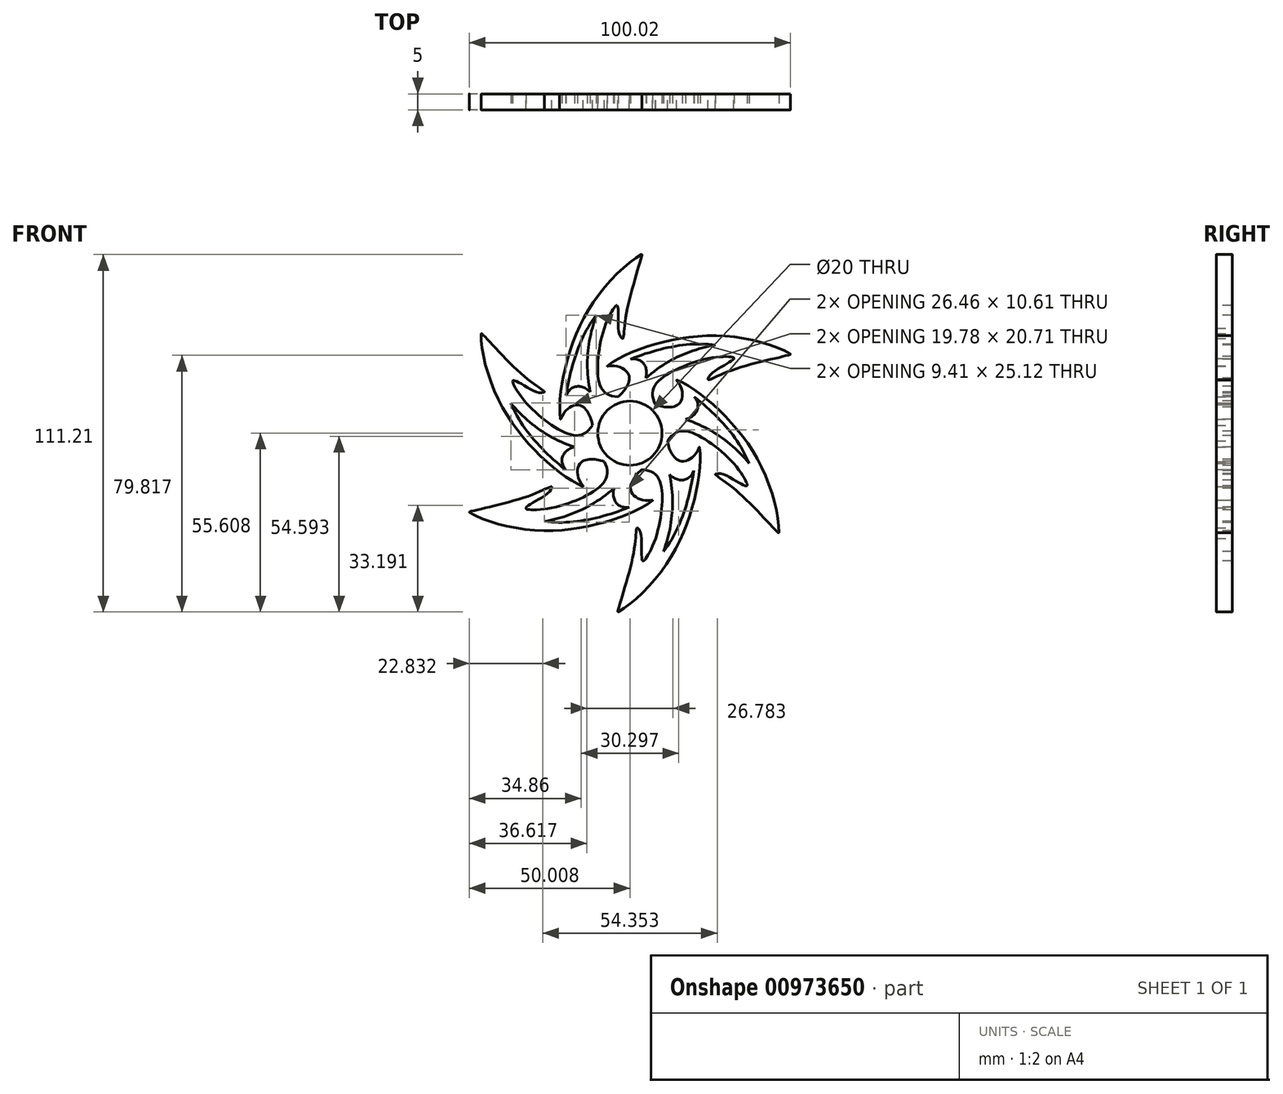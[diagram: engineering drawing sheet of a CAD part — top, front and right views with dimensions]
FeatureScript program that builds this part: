
annotation { "Feature Type Name" : "Feature", "Feature Type Description" : "" }
export const myFeature = defineFeature(function(context is Context, id is Id, definition is map)
    precondition{}
    {
        {
            var Q0;
            Q0=qCreatedBy(makeId("Front.planeOp"),FACE);
            var sketch = newSketch(context, id + "F0", { "sketchPlane" : qUnion([Q0])});
            skArc(sketch, "E0", {"start": v(51.43, 69.64) * mm, "mid": v(53.41, 47.38) * mm, "end": v(64.36, 66.87) * mm});
            skFitSpline(sketch, "E1", {"points": [v(51.43, 69.64) * mm, v(54.7, 73.05) * mm, v(55.5, 76.92) * mm, v(48.53, 79.55) * mm], "startDerivative": vector(15.23, 10.38) * mm, "endDerivative": vector(-26.97, -6.76) * mm});
            skFitSpline(sketch, "E2", {"points": [v(48.53, 79.55) * mm, v(62.9, 86.26) * mm, v(85.86, 89) * mm, v(106.01, 83.36) * mm], "startDerivative": vector(30.67, 25.16) * mm, "endDerivative": vector(38.45, -24.26) * mm});
            skFitSpline(sketch, "E3", {"points": [v(80.2, 75.5) * mm, v(87.2, 78.3) * mm, v(106.01, 83.36) * mm], "startDerivative": vector(3.98, -2.07) * mm, "endDerivative": vector(10.42, 3.53) * mm});
            skFitSpline(sketch, "E4", {"points": [v(80.2, 75.5) * mm, v(85.84, 80.3) * mm, v(88.27, 82.15) * mm, v(87.74, 82.5) * mm, v(80.2, 82.1) * mm], "startDerivative": vector(1.03, 17.3) * mm, "endDerivative": vector(-30.04, -5.32) * mm});
            skFitSpline(sketch, "E5", {"points": [v(80.2, 82.1) * mm, v(68.5, 77.72) * mm, v(63.22, 72.8) * mm, v(64.36, 66.87) * mm], "startDerivative": vector(-31.78, -6.94) * mm, "endDerivative": vector(15.18, -22.06) * mm});
            skSolve(sketch);
        }
        {
            var Q0;
            Q0=makeQuery(id+"F0.imprint","IMPRINT",FACE,{"disambiguationData":[TD([[makeQuery(id+"F0.imprint","IMPRINT",EDGE,{"derivedFrom":sQuery(id+"F0.wireOp",EDGE,"E0")}),1.0]])]});
            extrude(context, id + "F1", {"entities" : qUnion([Q0]), "flatOperationType" : FlatOperationType.REMOVE, "depth" : 5 * mm, "offsetDistance" : 25.4 * mm, "domain" : OperationDomain.MODEL});
        }
        {
            var Q0;
            Q0=makeQuery(id+"F1.opExtrude","SWEPT_EDGE",EDGE,{"disambiguationData":[OSD([sQuery(id+"F0.wireOp",EDGE,"E2"),sQuery(id+"F0.wireOp",EDGE,"E3")])]});
            var Q1;
            Q1=makeQuery(id+"F1.opExtrude","SWEPT_EDGE",EDGE,{"disambiguationData":[OSD([sQuery(id+"F0.wireOp",EDGE,"E3"),sQuery(id+"F0.wireOp",EDGE,"E4")])]});
            var Q2;
            Q2=makeQuery(id+"F1.opExtrude","SWEPT_EDGE",EDGE,{"disambiguationData":[OSD([sQuery(id+"F0.wireOp",EDGE,"E1"),sQuery(id+"F0.wireOp",EDGE,"E2")])]});
            var Q3;
            Q3=makeQuery(id+"F1.opExtrude","CAP_EDGE",EDGE,{"disambiguationData":[OSD([sQuery(id+"F0.wireOp",EDGE,"E0")])],"isStart":false});
            fillet(context, id + "F2", {"entities" : qUnion([Q0, Q1, Q2, Q3]), "radius" : 0.1 * mm, "tangentPropagation" : true, "allowEdgeOverflow" : false});
        }
        {
            var Q0;
            Q0=makeQuery(id+"F1.opExtrude","CAP_FACE",FACE,{"disambiguationData":[OSD([sQuery(id+"F0.wireOp",EDGE,"E0"),sQuery(id+"F0.wireOp",EDGE,"E1"),sQuery(id+"F0.wireOp",EDGE,"E2"),sQuery(id+"F0.wireOp",EDGE,"E3"),sQuery(id+"F0.wireOp",EDGE,"E4"),sQuery(id+"F0.wireOp",EDGE,"E5")])],"isStart":false});
            var sketch = newSketch(context, id + "F3", { "sketchPlane" : qUnion([Q0])});
            skFitSpline(sketch, "E6", {"points": [v(56.03, 81.84) * mm, v(60.8, 75.93) * mm], "startDerivative": vector(12.12, 1.85) * mm, "endDerivative": vector(-2.6, -9.8) * mm});
            skFitSpline(sketch, "E7", {"points": [v(60.8, 75.93) * mm, v(82.5, 86.25) * mm], "startDerivative": vector(19.58, 17.47) * mm, "endDerivative": vector(23.82, 4.23) * mm});
            skFitSpline(sketch, "E8", {"points": [v(56.03, 81.84) * mm, v(82.5, 86.25) * mm], "startDerivative": vector(26.46, 10.59) * mm, "endDerivative": vector(25.1, -3.47) * mm});
            skSolve(sketch);
        }
        {
            var Q0;
            Q0=makeQuery(id+"F3.imprint","IMPRINT",FACE,{"disambiguationData":[TD([[makeQuery(id+"F3.imprint","IMPRINT",EDGE,{"derivedFrom":sQuery(id+"F3.wireOp",EDGE,"E6")}),1.0]])]});
            extrude(context, id + "F4", {"entities" : qUnion([Q0]), "operationType" : NewBodyOperationType.REMOVE, "endBound" : BoundingType.THROUGH_ALL, "oppositeDirection" : true, "depth" : 25 * mm, "offsetDistance" : 25 * mm});
        }
        {
            var Q0;
            Q0=makeQuery(id+"F1.opExtrude","SWEPT_BODY",BODY,{"disambiguationData":[OSD([sQuery(id+"F0.wireOp",EDGE,"E0"),sQuery(id+"F0.wireOp",EDGE,"E1"),sQuery(id+"F0.wireOp",EDGE,"E2"),sQuery(id+"F0.wireOp",EDGE,"E3"),sQuery(id+"F0.wireOp",EDGE,"E4"),sQuery(id+"F0.wireOp",EDGE,"E5")])]});
            var Q1;
            Q1=makeQuery(id+"F1.opExtrude","SWEPT_FACE",FACE,{"disambiguationData":[OSD([sQuery(id+"F0.wireOp",EDGE,"E0")])]});
            circularPattern(context, id + "F5", {"operationType" : NewBodyOperationType.ADD, "entities" : qUnion([Q0]), "axis" : qUnion([Q1]), "angle" : 360 * degree, "instanceCount" : 6, "equalSpace" : true});
        }
        {
            var Q0;
            Q0=makeQuery(id+"F1.opExtrude","CAP_FACE",FACE,{"disambiguationData":[OSD([sQuery(id+"F0.wireOp",EDGE,"E0"),sQuery(id+"F0.wireOp",EDGE,"E1"),sQuery(id+"F0.wireOp",EDGE,"E2"),sQuery(id+"F0.wireOp",EDGE,"E3"),sQuery(id+"F0.wireOp",EDGE,"E4"),sQuery(id+"F0.wireOp",EDGE,"E5")])],"isStart":false});
            var sketch = newSketch(context, id + "F6", { "sketchPlane" : qUnion([Q0])});
            skCircle(sketch, "E9", {"center": v(55.87, 58.82) * mm, "radius": 10 * mm});
            skSolve(sketch);
        }
        {
            var Q0;
            Q0=makeQuery(id+"F6.imprint","IMPRINT",FACE,{"disambiguationData":[TD([[makeQuery(id+"F6.imprint","IMPRINT",EDGE,{"derivedFrom":sQuery(id+"F6.wireOp",EDGE,"E9")}),1.0]])]});
            extrude(context, id + "F7", {"entities" : qUnion([Q0]), "operationType" : NewBodyOperationType.REMOVE, "flatOperationType" : FlatOperationType.REMOVE, "endBound" : BoundingType.THROUGH_ALL, "oppositeDirection" : true, "depth" : 3 * mm, "offsetDistance" : 25 * mm, "domain" : OperationDomain.MODEL});
        }
    });
